# Revit family: Apollo 14
name_source: partatom
category: Lighting Fixtures
units: mm (PartAtom-declared; Revit-internal decimal feet)

## family parameters
Cut with Voids When Loaded = No
Host = Face
Light Source = Yes
Part Type = Normal
Room Calculation Point = No
Round Connector Dimension = Use Diameter
Shared = No

## types (1)
- Apollo 14
    ArticleNumber = 492214
    AssetType = Fixed installation
    Brand = Pholc
    Category = Wall lamp
    Class = Class 1
    Color = Aluminium
    Color Filter = 16777215
    Default Elevation = 1200 mm
    Dimming Lamp Color Temperature Shift = <None>
    ElectricalDeviceNominalPower = 10
    Emit from Line Length = 5 mm  [stored 0.0164042 ft]
    IFC classification = Light Fixture
    IP_Code = IP20
    Lamp = LED
    Light Source Symbol Length = 200 mm  [stored 0.656168 ft]
    LightFixtureMountingType = SURFACE
    LightFixturePlacingType = WALL
    Lightsource included = No
    Lightsource type = Gu10
    Manufacturer = Pholc
    ManufacturerName = Pholc
    ManufacturerURL = https://www.pholc.se
    Material = Aluminium
    Material Outer = Aluminum, Anodized Silver
    Model = Apollo 14
    ModelNumber = 492214
    NBS Reference Description = General Lighting Systems
    NBSReference = 70-80-33
    Name = Apollo 14
    Nominal Height = 144 mm
    Nominal Length = 178 mm  [stored 0.58399 ft]
    Nominal Width = 125 mm  [stored 0.410105 ft]
    NominalCurrent = 0 A
    NominalVoltage = 0 V
    Shape = Cone
    Size = 125x178x144
    Socket = Gu10
    Spot Beam Angle = 80.00°
    Spot Field Angle = 80.00°
    Tilt Angle = 90.00°
    TotalWattage = 15 W
    URL = https://www.pholc.se
    Uniclass2015Description = Surface luminaires
    Uniclass2015Reference = Pr_70_70_48_85
    VisualHusRef = Pholc_Id084
    Wattage Comments = 10

note: [stored X ft] marks values corroborated as IEEE doubles in the binary element streams (Revit-internal decimal feet)

## geometry (parser evidence)
native form markers: Sweep x3
no freeform markers — native parametric forms only
